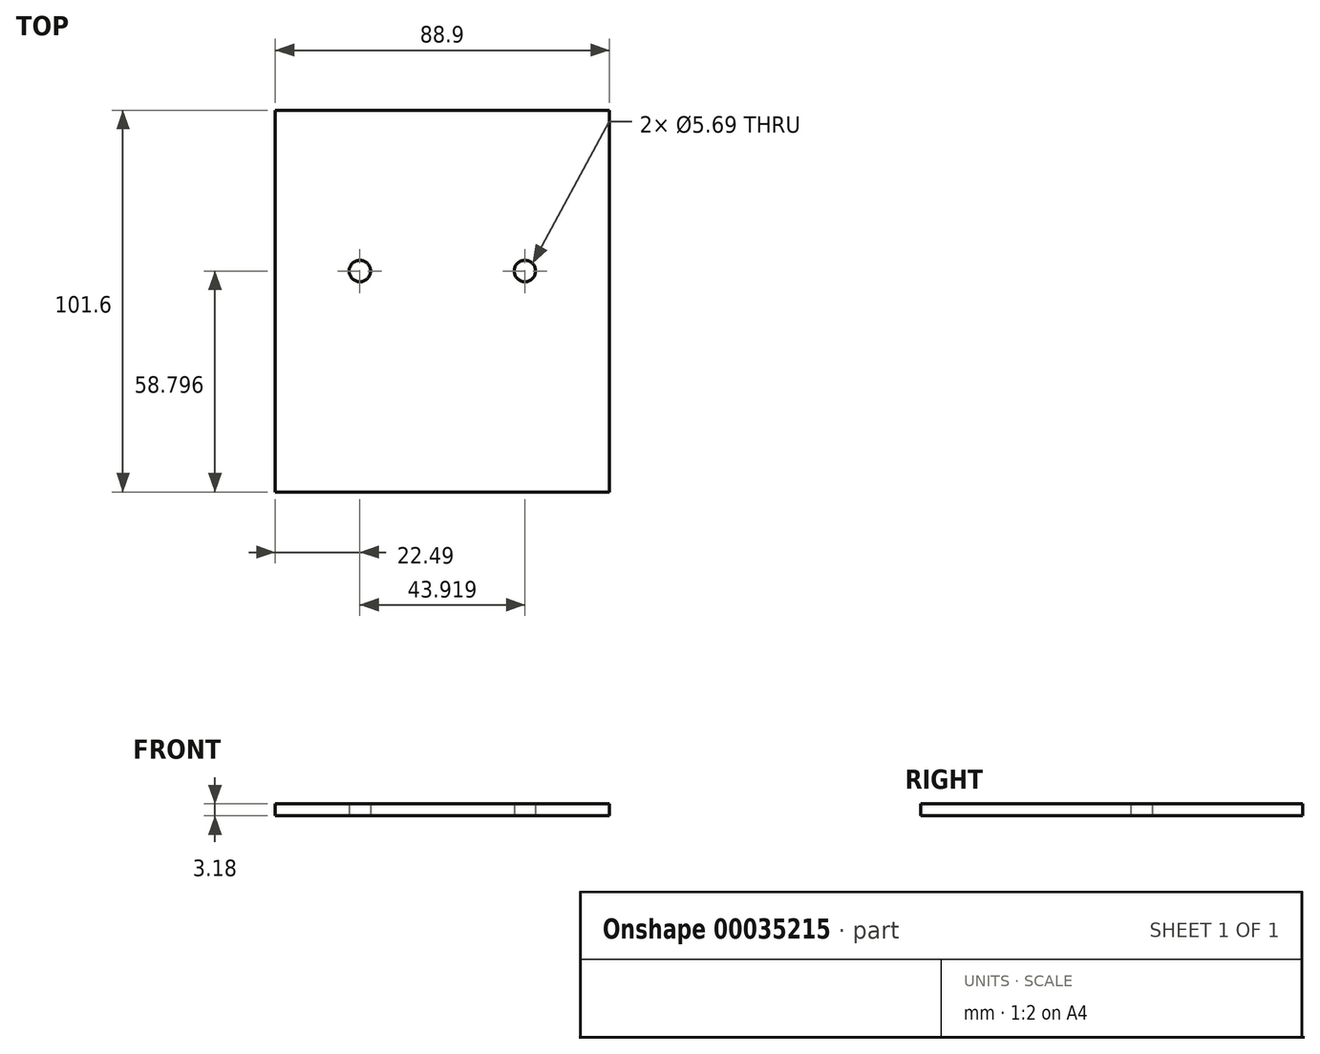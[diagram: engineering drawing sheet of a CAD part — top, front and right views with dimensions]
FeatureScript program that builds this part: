
annotation { "Feature Type Name" : "Feature", "Feature Type Description" : "" }
export const myFeature = defineFeature(function(context is Context, id is Id, definition is map)
    precondition{}
    {
        {
            var Q0;
            Q0=qCreatedBy(makeId("Top.planeOp"),FACE);
            var sketch = newSketch(context, id + "F0", { "sketchPlane" : qUnion([Q0])});
            skLineSegment(sketch, "E0.rect.bottom", {"start": v(-44.45, 50.8) * mm, "end": v(44.45, 50.8) * mm});
            skLineSegment(sketch, "E0.rect.top", {"start": v(-44.45, -50.8) * mm, "end": v(44.45, -50.8) * mm});
            skLineSegment(sketch, "E0.rect.left", {"start": v(-44.45, 50.8) * mm, "end": v(-44.45, -50.8) * mm});
            skLineSegment(sketch, "E0.rect.right", {"start": v(44.45, 50.8) * mm, "end": v(44.45, -50.8) * mm});
            skPoint(sketch, "E0.rect.middle", {"position": v(0, 0) * mm});
            skLineSegment(sketch, "E1", {"start": v(0, 50.8) * mm, "end": v(0, -50.8) * mm, "construction": true});
            skLineSegment(sketch, "E2", {"start": v(44.45, 0) * mm, "end": v(-44.45, 0) * mm, "construction": true});
            skCircle(sketch, "E3", {"center": v(21.96, 8) * mm, "radius": 10.25 * mm});
            skCircle(sketch, "E4.MirrorC", {"center": v(-21.96, 8) * mm, "radius": 10.25 * mm});
            skCircle(sketch, "E5", {"center": v(21.96, 8) * mm, "radius": 2.84 * mm});
            skCircle(sketch, "E6.MirrorC", {"center": v(-21.96, 8) * mm, "radius": 2.84 * mm});
            skCircle(sketch, "E7", {"center": v(-21.96, 8) * mm, "radius": 18.29 * mm});
            skCircle(sketch, "E8.MirrorC", {"center": v(21.96, 8) * mm, "radius": 18.29 * mm});
            skSolve(sketch);
        }
        {
            var Q0;
            Q0=makeQuery(id+"F0.imprint","IMPRINT",FACE,{"disambiguationData":[TD([[makeQuery(id+"F0.imprint","IMPRINT",EDGE,{"derivedFrom":sQuery(id+"F0.wireOp",EDGE,"E4.MirrorC")}),-1.0]])]});
            var Q1;
            Q1=makeQuery(id+"F0.imprint","IMPRINT",FACE,{"disambiguationData":[TD([[makeQuery(id+"F0.imprint","IMPRINT",EDGE,{"derivedFrom":sQuery(id+"F0.wireOp",EDGE,"E4.MirrorC")}),1.0]])]});
            var Q2;
            Q2=makeQuery(id+"F0.imprint","IMPRINT",FACE,{"disambiguationData":[TD([[makeQuery(id+"F0.imprint","IMPRINT",EDGE,{"derivedFrom":sQuery(id+"F0.wireOp",EDGE,"E0.rect.bottom")}),-1.0]])]});
            var Q3;
            Q3=makeQuery(id+"F0.imprint","IMPRINT",FACE,{"disambiguationData":[TD([[makeQuery(id+"F0.imprint","IMPRINT",EDGE,{"derivedFrom":sQuery(id+"F0.wireOp",EDGE,"E3")}),-1.0]])]});
            var Q4;
            Q4=makeQuery(id+"F0.imprint","IMPRINT",FACE,{"disambiguationData":[TD([[makeQuery(id+"F0.imprint","IMPRINT",EDGE,{"derivedFrom":sQuery(id+"F0.wireOp",EDGE,"E3")}),1.0]])]});
            extrude(context, id + "F1", {"entities" : qUnion([Q0, Q1, Q2, Q3, Q4]), "depth" : 3.17 * mm});
        }
    });
